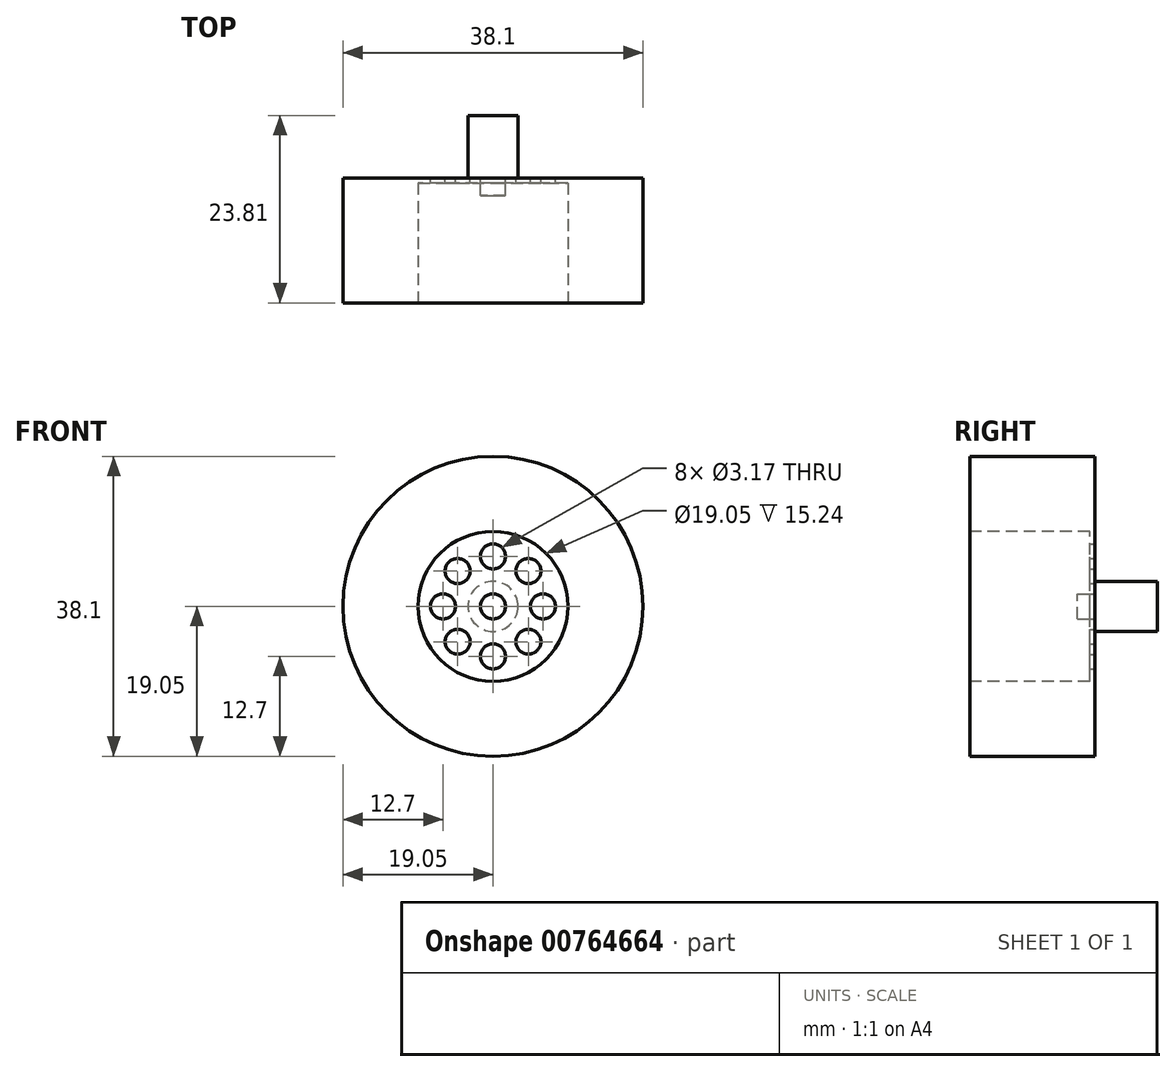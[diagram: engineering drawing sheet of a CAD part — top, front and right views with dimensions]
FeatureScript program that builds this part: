
annotation { "Feature Type Name" : "Feature", "Feature Type Description" : "" }
export const myFeature = defineFeature(function(context is Context, id is Id, definition is map)
    precondition{}
    {
        {
            var Q0;
            Q0=qCreatedBy(makeId("Front.planeOp"),FACE);
            var sketch = newSketch(context, id + "F0", { "sketchPlane" : qUnion([Q0])});
            skCircle(sketch, "E0", {"center": v(0, 0) * mm, "radius": 19.05 * mm});
            skSolve(sketch);
        }
        {
            var Q0;
            Q0=makeQuery(id+"F0.imprint","IMPRINT",FACE,{"disambiguationData":[TD([[makeQuery(id+"F0.imprint","IMPRINT",EDGE,{"derivedFrom":sQuery(id+"F0.wireOp",EDGE,"E0")}),1.0]])]});
            var sketch = newSketch(context, id + "F1", { "sketchPlane" : qUnion([Q0])});
            skCircle(sketch, "E1", {"center": v(0, 0) * mm, "radius": 9.53 * mm});
            skSolve(sketch);
        }
        {
            var Q0;
            Q0=makeQuery(id+"F0.imprint","IMPRINT",FACE,{"disambiguationData":[TD([[makeQuery(id+"F0.imprint","IMPRINT",EDGE,{"derivedFrom":sQuery(id+"F0.wireOp",EDGE,"E0")}),1.0]])]});
            extrude(context, id + "F2", {"entities" : qUnion([Q0]), "oppositeDirection" : true, "depth" : 15.88 * mm, "offsetDistance" : 25.4 * mm});
        }
        {
            var Q0;
            Q0=makeQuery(id+"F1.imprint","IMPRINT",FACE,{"disambiguationData":[TD([[makeQuery(id+"F1.imprint","IMPRINT",EDGE,{"derivedFrom":sQuery(id+"F1.wireOp",EDGE,"E1")}),1.0]])]});
            extrude(context, id + "F3", {"entities" : qUnion([Q0]), "operationType" : NewBodyOperationType.REMOVE, "oppositeDirection" : true, "depth" : 15.24 * mm, "offsetDistance" : 25.4 * mm});
        }
        {
            var Q0;
            Q0=makeQuery(id+"F3.boolean.opBoolean","COPY",FACE,{"derivedFrom":makeQuery(id+"F3.opExtrude","CAP_FACE",FACE,{"disambiguationData":[OSD([sQuery(id+"F1.wireOp",EDGE,"E1")])],"isStart":false})});
            var sketch = newSketch(context, id + "F4", { "sketchPlane" : qUnion([Q0])});
            skCircle(sketch, "E2", {"center": v(0, 0) * mm, "radius": 1.59 * mm});
            skSolve(sketch);
        }
        {
            var Q0;
            Q0=makeQuery(id+"F4.imprint","IMPRINT",FACE,{"disambiguationData":[TD([[makeQuery(id+"F4.imprint","IMPRINT",EDGE,{"derivedFrom":sQuery(id+"F4.wireOp",EDGE,"E2")}),1.0]])]});
            extrude(context, id + "F5", {"entities" : qUnion([Q0]), "operationType" : NewBodyOperationType.ADD, "depth" : 1.59 * mm, "offsetDistance" : 25.4 * mm});
        }
        {
            var Q0;
            Q0=makeQuery(id+"F2.opExtrude","CAP_FACE",FACE,{"disambiguationData":[OSD([sQuery(id+"F0.wireOp",EDGE,"E0")])],"isStart":false});
            var sketch = newSketch(context, id + "F6", { "sketchPlane" : qUnion([Q0])});
            skCircle(sketch, "E3", {"center": v(0, 0) * mm, "radius": 3.18 * mm});
            skSolve(sketch);
        }
        {
            var Q0;
            Q0=makeQuery(id+"F6.imprint","IMPRINT",FACE,{"disambiguationData":[TD([[makeQuery(id+"F6.imprint","IMPRINT",EDGE,{"derivedFrom":sQuery(id+"F6.wireOp",EDGE,"E3")}),1.0]])]});
            extrude(context, id + "F7", {"entities" : qUnion([Q0]), "operationType" : NewBodyOperationType.ADD, "depth" : 7.94 * mm, "offsetDistance" : 25.4 * mm});
        }
        {
            var Q0;
            Q0=makeQuery(id+"F2.opExtrude","CAP_FACE",FACE,{"disambiguationData":[OSD([sQuery(id+"F0.wireOp",EDGE,"E0")])],"isStart":false});
            var sketch = newSketch(context, id + "F8", { "sketchPlane" : qUnion([Q0])});
            skCircle(sketch, "E4", {"center": v(0, 0) * mm, "radius": 8.73 * mm});
            skSolve(sketch);
        }
        {
            var Q0;
            Q0=makeQuery(id+"F8.imprint","IMPRINT",FACE,{"disambiguationData":[TD([[makeQuery(id+"F8.imprint","IMPRINT",EDGE,{"derivedFrom":sQuery(id+"F8.wireOp",EDGE,"E4")}),1.0]])]});
            var sketch = newSketch(context, id + "F9", { "sketchPlane" : qUnion([Q0])});
            skCircle(sketch, "E5", {"center": v(6.35, 0) * mm, "radius": 1.59 * mm});
            skCircle(sketch, "E6.1.0", {"center": v(4.5, 4.5) * mm, "radius": 1.59 * mm});
            skCircle(sketch, "E6.2.0", {"center": v(0, 6.35) * mm, "radius": 1.59 * mm});
            skCircle(sketch, "E6.3.0", {"center": v(-4.5, 4.5) * mm, "radius": 1.59 * mm});
            skCircle(sketch, "E6.4.0", {"center": v(-6.35, 0) * mm, "radius": 1.59 * mm});
            skCircle(sketch, "E6.5.0", {"center": v(-4.5, -4.5) * mm, "radius": 1.59 * mm});
            skCircle(sketch, "E6.6.0", {"center": v(0, -6.35) * mm, "radius": 1.59 * mm});
            skCircle(sketch, "E6.7.0", {"center": v(4.5, -4.5) * mm, "radius": 1.59 * mm});
            skPoint(sketch, "E6.center", {"position": v(0, 0) * mm});
            skSolve(sketch);
        }
        {
            var Q0;
            Q0 = qSketchRegion(id + "F9", true);
            extrude(context, id + "F10", {"entities" : qUnion([Q0]), "operationType" : NewBodyOperationType.REMOVE, "oppositeDirection" : true, "depth" : 25.4 * mm, "offsetDistance" : 25.4 * mm});
        }
    });
